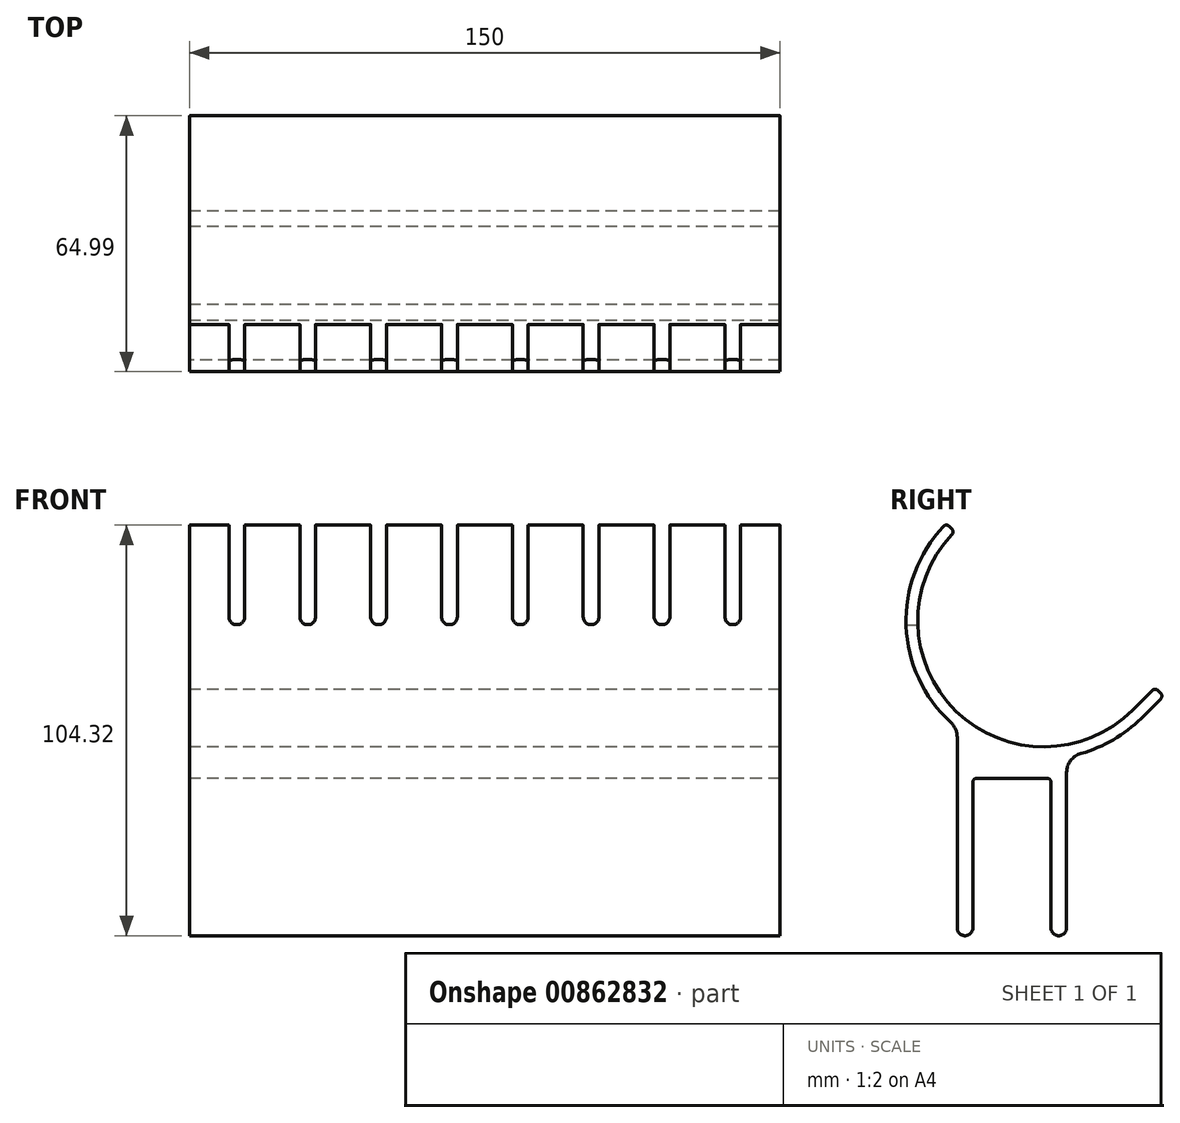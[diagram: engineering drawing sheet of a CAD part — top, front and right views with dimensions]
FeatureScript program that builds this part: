
annotation { "Feature Type Name" : "Feature", "Feature Type Description" : "" }
export const myFeature = defineFeature(function(context is Context, id is Id, definition is map)
    precondition{}
    {
        {
            var Q0;
            Q0=qCreatedBy(makeId("Right.planeOp"),FACE);
            var sketch = newSketch(context, id + "F0", { "sketchPlane" : qUnion([Q0])});
            skLineSegment(sketch, "E0", {"start": v(1, 40) * mm, "end": v(18.8, 40) * mm});
            skLineSegment(sketch, "E1", {"start": v(19.8, 39) * mm, "end": v(19.8, 2) * mm});
            skLineSegment(sketch, "E2", {"start": v(21.8, 0) * mm, "end": v(21.8, 0) * mm});
            skLineSegment(sketch, "E3", {"start": v(23.8, 2) * mm, "end": v(23.8, 41.49) * mm});
            skLineSegment(sketch, "E4", {"start": v(0, 39) * mm, "end": v(0, 2) * mm});
            skLineSegment(sketch, "E5", {"start": v(-2, 0) * mm, "end": v(-2, 0) * mm});
            skLineSegment(sketch, "E6", {"start": v(-4, 2) * mm, "end": v(-4, 50.49) * mm});
            skArc(sketch, "E7", {"start": v(-5.3, 101.93) * mm, "mid": v(-4.28, 57.03) * mm, "end": v(40.63, 57.37) * mm});
            skArc(sketch, "E8", {"start": v(27.45, 46.3) * mm, "mid": v(35.68, 49.8) * mm, "end": v(42.75, 55.25) * mm});
            skLineSegment(sketch, "E9", {"start": v(-6.03, 104.03) * mm, "end": v(-5.32, 103.32) * mm});
            skArc(sketch, "E10.trimOffspring", {"start": v(-7.47, 104.01) * mm, "mid": v(-16.98, 78.7) * mm, "end": v(-5.63, 54.18) * mm});
            skPoint(sketch, "E11.visualSharp", {"position": v(-4, 52.78) * mm});
            skArc(sketch, "E11.filletArc", {"start": v(-4, 50.49) * mm, "mid": v(-4.42, 52.5) * mm, "end": v(-5.63, 54.18) * mm});
            skPoint(sketch, "E12.visualSharp", {"position": v(23.8, 45.48) * mm});
            skArc(sketch, "E12.filletArc", {"start": v(27.45, 46.3) * mm, "mid": v(24.82, 44.5) * mm, "end": v(23.8, 41.49) * mm});
            skPoint(sketch, "E13.visualSharp", {"position": v(0, 40) * mm});
            skArc(sketch, "E13.filletArc", {"start": v(1, 40) * mm, "mid": v(0.3, 39.7) * mm, "end": v(0, 39) * mm});
            skPoint(sketch, "E14.visualSharp", {"position": v(19.8, 40) * mm});
            skArc(sketch, "E14.filletArc", {"start": v(19.8, 39) * mm, "mid": v(19.5, 39.7) * mm, "end": v(18.8, 40) * mm});
            skPoint(sketch, "E15.visualSharp", {"position": v(-4, 0) * mm});
            skArc(sketch, "E15.filletArc", {"start": v(-4, 2) * mm, "mid": v(-3.41, 0.59) * mm, "end": v(-2, 0) * mm});
            skPoint(sketch, "E16.visualSharp", {"position": v(0, 0) * mm});
            skArc(sketch, "E16.filletArc", {"start": v(-2, 0) * mm, "mid": v(-0.59, 0.59) * mm, "end": v(0, 2) * mm});
            skPoint(sketch, "E17.visualSharp", {"position": v(19.8, 0) * mm});
            skArc(sketch, "E17.filletArc", {"start": v(19.8, 2) * mm, "mid": v(20.39, 0.59) * mm, "end": v(21.8, 0) * mm});
            skPoint(sketch, "E18.visualSharp", {"position": v(23.8, 0) * mm});
            skArc(sketch, "E18.filletArc", {"start": v(21.8, 0) * mm, "mid": v(23.21, 0.59) * mm, "end": v(23.8, 2) * mm});
            skLineSegment(sketch, "E19", {"start": v(40.63, 57.37) * mm, "end": v(45.58, 62.32) * mm});
            skLineSegment(sketch, "E20", {"start": v(47, 62.32) * mm, "end": v(47.7, 61.62) * mm});
            skLineSegment(sketch, "E21", {"start": v(47.7, 60.2) * mm, "end": v(42.75, 55.25) * mm});
            skPoint(sketch, "E22.visualSharp", {"position": v(-6.75, 104.75) * mm});
            skArc(sketch, "E22.filletArc", {"start": v(-6.03, 104.03) * mm, "mid": v(-6.75, 104.32) * mm, "end": v(-7.47, 104.01) * mm});
            skPoint(sketch, "E23.visualSharp", {"position": v(-4.63, 102.63) * mm});
            skArc(sketch, "E23.filletArc", {"start": v(-5.3, 101.93) * mm, "mid": v(-5.03, 102.63) * mm, "end": v(-5.32, 103.32) * mm});
            skPoint(sketch, "E24.visualSharp", {"position": v(46.28, 63.03) * mm});
            skArc(sketch, "E24.filletArc", {"start": v(47, 62.32) * mm, "mid": v(46.28, 62.62) * mm, "end": v(45.58, 62.32) * mm});
            skPoint(sketch, "E25.visualSharp", {"position": v(48.4, 60.9) * mm});
            skArc(sketch, "E25.filletArc", {"start": v(47.7, 60.2) * mm, "mid": v(48, 60.9) * mm, "end": v(47.7, 61.62) * mm});
            skSolve(sketch);
        }
        {
            var Q0;
            Q0=makeQuery(id+"F0.imprint","IMPRINT",FACE,{"disambiguationData":[TD([[makeQuery(id+"F0.imprint","IMPRINT",EDGE,{"derivedFrom":sQuery(id+"F0.wireOp",EDGE,"E0")}),1.0]])]});
            extrude(context, id + "F1", {"entities" : qUnion([Q0]), "depth" : 150 * mm, "offsetDistance" : 25 * mm});
        }
        {
            var Q0;
            Q0=qCreatedBy(makeId("Front.planeOp"),FACE);
            var sketch = newSketch(context, id + "F2", { "sketchPlane" : qUnion([Q0])});
            skLineSegment(sketch, "E26.bottom", {"start": v(10, 114.01) * mm, "end": v(14, 114.01) * mm});
            skLineSegment(sketch, "E26.top", {"start": v(12, 79.01) * mm, "end": v(12, 79.01) * mm});
            skLineSegment(sketch, "E26.left", {"start": v(10, 114.01) * mm, "end": v(10, 81.01) * mm});
            skLineSegment(sketch, "E26.right", {"start": v(14, 114.01) * mm, "end": v(14, 81.01) * mm});
            skPoint(sketch, "E27.visualSharp", {"position": v(10, 79.01) * mm});
            skArc(sketch, "E27.filletArc", {"start": v(10, 81.01) * mm, "mid": v(10.59, 79.6) * mm, "end": v(12, 79.01) * mm});
            skPoint(sketch, "E28.visualSharp", {"position": v(14, 79.01) * mm});
            skArc(sketch, "E28.filletArc", {"start": v(12, 79.01) * mm, "mid": v(13.41, 79.6) * mm, "end": v(14, 81.01) * mm});
            skPoint(sketch, "E29.1.0.0", {"position": v(28, 79.01) * mm});
            skPoint(sketch, "E29.1.0.1", {"position": v(32, 79.01) * mm});
            skLineSegment(sketch, "E29.1.0.2", {"start": v(32, 114.01) * mm, "end": v(32, 81.01) * mm});
            skLineSegment(sketch, "E29.1.0.3", {"start": v(28, 114.01) * mm, "end": v(32, 114.01) * mm});
            skLineSegment(sketch, "E29.1.0.4", {"start": v(28, 114.01) * mm, "end": v(28, 81.01) * mm});
            skArc(sketch, "E29.1.0.5", {"start": v(28, 81.01) * mm, "mid": v(28.59, 79.6) * mm, "end": v(30, 79.01) * mm});
            skArc(sketch, "E29.1.0.6", {"start": v(30, 79.01) * mm, "mid": v(31.41, 79.6) * mm, "end": v(32, 81.01) * mm});
            skPoint(sketch, "E29.2.0.0", {"position": v(46, 79.01) * mm});
            skPoint(sketch, "E29.2.0.1", {"position": v(50, 79.01) * mm});
            skLineSegment(sketch, "E29.2.0.2", {"start": v(50, 114.01) * mm, "end": v(50, 81.01) * mm});
            skLineSegment(sketch, "E29.2.0.3", {"start": v(46, 114.01) * mm, "end": v(50, 114.01) * mm});
            skLineSegment(sketch, "E29.2.0.4", {"start": v(46, 114.01) * mm, "end": v(46, 81.01) * mm});
            skArc(sketch, "E29.2.0.5", {"start": v(46, 81.01) * mm, "mid": v(46.59, 79.6) * mm, "end": v(48, 79.01) * mm});
            skArc(sketch, "E29.2.0.6", {"start": v(48, 79.01) * mm, "mid": v(49.41, 79.6) * mm, "end": v(50, 81.01) * mm});
            skPoint(sketch, "E29.3.0.0", {"position": v(64, 79.01) * mm});
            skPoint(sketch, "E29.3.0.1", {"position": v(68, 79.01) * mm});
            skLineSegment(sketch, "E29.3.0.2", {"start": v(68, 114.01) * mm, "end": v(68, 81.01) * mm});
            skLineSegment(sketch, "E29.3.0.3", {"start": v(64, 114.01) * mm, "end": v(68, 114.01) * mm});
            skLineSegment(sketch, "E29.3.0.4", {"start": v(64, 114.01) * mm, "end": v(64, 81.01) * mm});
            skArc(sketch, "E29.3.0.5", {"start": v(64, 81.01) * mm, "mid": v(64.59, 79.6) * mm, "end": v(66, 79.01) * mm});
            skArc(sketch, "E29.3.0.6", {"start": v(66, 79.01) * mm, "mid": v(67.41, 79.6) * mm, "end": v(68, 81.01) * mm});
            skPoint(sketch, "E29.4.0.0", {"position": v(82, 79.01) * mm});
            skPoint(sketch, "E29.4.0.1", {"position": v(86, 79.01) * mm});
            skLineSegment(sketch, "E29.4.0.2", {"start": v(86, 114.01) * mm, "end": v(86, 81.01) * mm});
            skLineSegment(sketch, "E29.4.0.3", {"start": v(82, 114.01) * mm, "end": v(86, 114.01) * mm});
            skLineSegment(sketch, "E29.4.0.4", {"start": v(82, 114.01) * mm, "end": v(82, 81.01) * mm});
            skArc(sketch, "E29.4.0.5", {"start": v(82, 81.01) * mm, "mid": v(82.59, 79.6) * mm, "end": v(84, 79.01) * mm});
            skArc(sketch, "E29.4.0.6", {"start": v(84, 79.01) * mm, "mid": v(85.41, 79.6) * mm, "end": v(86, 81.01) * mm});
            skPoint(sketch, "E29.5.0.0", {"position": v(100, 79.01) * mm});
            skPoint(sketch, "E29.5.0.1", {"position": v(104, 79.01) * mm});
            skLineSegment(sketch, "E29.5.0.2", {"start": v(104, 114.01) * mm, "end": v(104, 81.01) * mm});
            skLineSegment(sketch, "E29.5.0.3", {"start": v(100, 114.01) * mm, "end": v(104, 114.01) * mm});
            skLineSegment(sketch, "E29.5.0.4", {"start": v(100, 114.01) * mm, "end": v(100, 81.01) * mm});
            skArc(sketch, "E29.5.0.5", {"start": v(100, 81.01) * mm, "mid": v(100.59, 79.6) * mm, "end": v(102, 79.01) * mm});
            skArc(sketch, "E29.5.0.6", {"start": v(102, 79.01) * mm, "mid": v(103.41, 79.6) * mm, "end": v(104, 81.01) * mm});
            skPoint(sketch, "E29.6.0.0", {"position": v(118, 79.01) * mm});
            skPoint(sketch, "E29.6.0.1", {"position": v(122, 79.01) * mm});
            skLineSegment(sketch, "E29.6.0.2", {"start": v(122, 114.01) * mm, "end": v(122, 81.01) * mm});
            skLineSegment(sketch, "E29.6.0.3", {"start": v(118, 114.01) * mm, "end": v(122, 114.01) * mm});
            skLineSegment(sketch, "E29.6.0.4", {"start": v(118, 114.01) * mm, "end": v(118, 81.01) * mm});
            skArc(sketch, "E29.6.0.5", {"start": v(118, 81.01) * mm, "mid": v(118.59, 79.6) * mm, "end": v(120, 79.01) * mm});
            skArc(sketch, "E29.6.0.6", {"start": v(120, 79.01) * mm, "mid": v(121.41, 79.6) * mm, "end": v(122, 81.01) * mm});
            skPoint(sketch, "E29.7.0.0", {"position": v(136, 79.01) * mm});
            skPoint(sketch, "E29.7.0.1", {"position": v(140, 79.01) * mm});
            skLineSegment(sketch, "E29.7.0.2", {"start": v(140, 114.01) * mm, "end": v(140, 81.01) * mm});
            skLineSegment(sketch, "E29.7.0.3", {"start": v(136, 114.01) * mm, "end": v(140, 114.01) * mm});
            skLineSegment(sketch, "E29.7.0.4", {"start": v(136, 114.01) * mm, "end": v(136, 81.01) * mm});
            skArc(sketch, "E29.7.0.5", {"start": v(136, 81.01) * mm, "mid": v(136.59, 79.6) * mm, "end": v(138, 79.01) * mm});
            skArc(sketch, "E29.7.0.6", {"start": v(138, 79.01) * mm, "mid": v(139.41, 79.6) * mm, "end": v(140, 81.01) * mm});
            skLineSegment(sketch, "E29.direction1", {"start": v(10, 79.01) * mm, "end": v(28, 79.01) * mm, "construction": true});
            skSolve(sketch);
        }
        {
            var Q0;
            Q0=makeQuery(id+"F2.imprint","IMPRINT",FACE,{"disambiguationData":[TD([[makeQuery(id+"F2.imprint","IMPRINT",EDGE,{"derivedFrom":sQuery(id+"F2.wireOp",EDGE,"E26.bottom")}),-1.0]])]});
            var Q1;
            Q1=makeQuery(id+"F2.imprint","IMPRINT",FACE,{"disambiguationData":[TD([[makeQuery(id+"F2.imprint","IMPRINT",EDGE,{"derivedFrom":sQuery(id+"F2.wireOp",EDGE,"E29.1.0.2")}),-1.0]])]});
            var Q2;
            Q2=makeQuery(id+"F2.imprint","IMPRINT",FACE,{"disambiguationData":[TD([[makeQuery(id+"F2.imprint","IMPRINT",EDGE,{"derivedFrom":sQuery(id+"F2.wireOp",EDGE,"E29.2.0.2")}),-1.0]])]});
            var Q3;
            Q3=makeQuery(id+"F2.imprint","IMPRINT",FACE,{"disambiguationData":[TD([[makeQuery(id+"F2.imprint","IMPRINT",EDGE,{"derivedFrom":sQuery(id+"F2.wireOp",EDGE,"E29.3.0.2")}),-1.0]])]});
            var Q4;
            Q4=makeQuery(id+"F2.imprint","IMPRINT",FACE,{"disambiguationData":[TD([[makeQuery(id+"F2.imprint","IMPRINT",EDGE,{"derivedFrom":sQuery(id+"F2.wireOp",EDGE,"E29.4.0.2")}),-1.0]])]});
            var Q5;
            Q5=makeQuery(id+"F2.imprint","IMPRINT",FACE,{"disambiguationData":[TD([[makeQuery(id+"F2.imprint","IMPRINT",EDGE,{"derivedFrom":sQuery(id+"F2.wireOp",EDGE,"E29.5.0.2")}),-1.0]])]});
            var Q6;
            Q6=makeQuery(id+"F2.imprint","IMPRINT",FACE,{"disambiguationData":[TD([[makeQuery(id+"F2.imprint","IMPRINT",EDGE,{"derivedFrom":sQuery(id+"F2.wireOp",EDGE,"E29.6.0.2")}),-1.0]])]});
            var Q7;
            Q7=makeQuery(id+"F2.imprint","IMPRINT",FACE,{"disambiguationData":[TD([[makeQuery(id+"F2.imprint","IMPRINT",EDGE,{"derivedFrom":sQuery(id+"F2.wireOp",EDGE,"E29.7.0.2")}),-1.0]])]});
            extrude(context, id + "F3", {"entities" : qUnion([Q0, Q1, Q2, Q3, Q4, Q5, Q6, Q7]), "operationType" : NewBodyOperationType.REMOVE, "depth" : 25 * mm, "offsetDistance" : 25 * mm});
        }
    });
